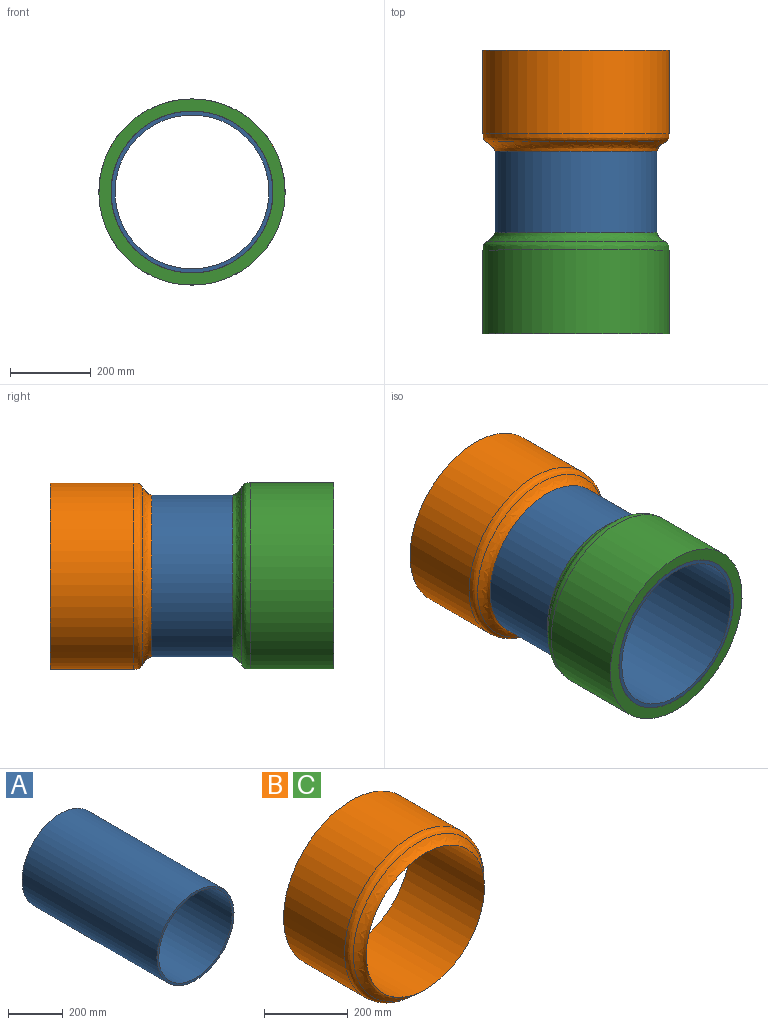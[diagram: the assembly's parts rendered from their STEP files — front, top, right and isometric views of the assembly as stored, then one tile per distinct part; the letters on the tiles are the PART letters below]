
ASSEMBLY  parts=3 mates=3
PART A: 4 faces, bbox 400x700x400 mm
  f0: cylinder r=190mm len=700mm, axis (0,1,0), area 835663.6mm2, adj f2,f3
  f1: cylinder r=200mm len=700mm, axis (0,1,0), area 879645.9mm2, adj f2,f3
  f2: plane 400x400mm, normal (0,-1,0), area 12252.2mm2, adj f0,f1
  f3: plane 400x400mm, normal (0,1,0), area 12252.2mm2, adj f0,f1
PART B: 5 faces, bbox 460x250x460 mm
  f0: cylinder r=230mm len=460mm, axis (0,-1,0), area 298439.7mm2, adj f1,f4
  f1: revolved ~460x460mm, area 33782.5mm2, adj f0,f2
  f2: revolved ~440.67x440.67mm, area 42096.9mm2, adj f1,f3
  f3: cylinder r=200mm len=400mm, axis (0,-1,0), area 314159.3mm2, adj f2,f4
  f4: plane 460x460mm, normal (0,1,0), area 40526.5mm2, adj f0,f3
PART C: same geometry as B
PLACE A rot(axis=(1,-0.03,0.03),0deg) t=(75.31,-658.03,8.23)mm fixed
PLACE B rot(axis=(1,-0.03,0.03),0deg) t=(75.31,-884.55,25.71)mm fixed
PLACE C rot(axis=(-1,0,0),180deg) t=(75.31,-1131.52,-9.25)mm
MATE revolute C.f0 <-> A.f1  axis (0,1,0) through (75.31,-1108.03,8.23)mm
MATE revolute B.f0 <-> A.f1  axis (0,-1,0) through (75.31,-783.03,8.23)mm
MATE parallel B.f0 <-> A.f0  axis (0,-1,0) through (75.31,-908.03,8.23)mm
